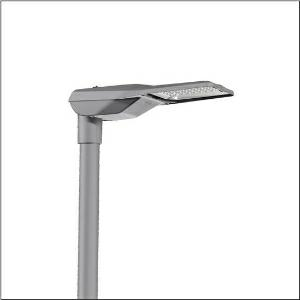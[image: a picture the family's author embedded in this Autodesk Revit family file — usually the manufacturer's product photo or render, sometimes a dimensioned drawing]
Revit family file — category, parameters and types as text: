
# Revit family: streetlight_sl_21_mini___pl52_5xe2h33s08hb_6ab9
name_source: partatom
category: Lighting Fixtures
units: mm (PartAtom-declared; Revit-internal decimal feet)

## family parameters
Cut with Voids When Loaded = No
Host = Face
Light Source = No
Part Type = Normal
Room Calculation Point = No
Round Connector Dimension = Use Diameter
Shared = No

## types (1)
- --- (1 x LED, 8890 lm, 66 W, 3000K)
    Apparent Load = 66 VA
    CIE Flux Codes = 27 59 98 100 100
    Color Rendering = 70
    Color Temperature = 3000K
    Default Elevation = 1800 mm
    Description = Streetlight SL 21 mini, mast luminaire, primary light control with lens, of PMMA, primary optical cover: cover, of toughened safety glass, transparent, light distribution: PL52, light emission: direct distribution, primary light characteristic: asymmetric, installation type: side-entry, post-top, LED, High Power LED, rated luminous flux: 8.890lm, luminous efficacy: 135lm/W, light colour: 730, colour temperature: 3000K, control gear: D4i, control: overheat protection, constant luminous flux control, time-dependent luminous flux control, flexible luminous flux parameterisation, pre-setting: logarithmic dimming characteristic, mains connection: 220..240V, AC, 50/60Hz, start of lifetime: 66W, end of service life: 69W, reduction: 30W, luminaire housing, of diecast aluminium, powder-coated, SITECO metallic grey (DB 702S), corrosivity category C5 high according to DIN EN ISO 12944, please order mast flange separately, inclination adjustable: 0°, 5°, 10°, 15°, sealing non-destructively replaceable, multi-level sealing system, length: 628mm, width: 235mm, height: 110mm, mast flange for spigot size: 42mm (side-entry): 5XC10008XM4, 60/48mm (side-entry/post-top): 5XC10108XM2, 76/60mm (side-entry/post-top): 5XC10108XM1, mounting height: 4..8m, Smart Interface above, protection rating (complete): IP66, insulation class (complete): insulation class II (safety insulation), certification: CE, ENEC, ENEC+, VDE, impact resistance: IK10, permissible operating ambient temperature for outdoor applications: -40..+50°C, standard-compliant lighting for roads and squares, packaging unit: 1 piece

Light Distribution: PL52
    Height = 110 mm
    Lamp = 1 x LED
    Lamp Light Flux = 8890 lm
    Lamp Power = 66 W
    Lamp count = 1
    Length = 625 mm
    Luminous efficacy = 135 lm/W
    Manufacturer = Siteco
    ModVariant = No
    Model = 5XE2H33S08HB
    Number of Poles = 1
    OnlyDefault = Yes
    Power Factor = 1
    Product Name = Streetlight SL 21 mini | PL52
    Product group = mast luminaire | pylon top
    ProductGroupID = 6100
    Protection Class = Protection class II
    Protection Degree = IP 66
    RLX_Detail_Level = 1
    RLX_Emergency_Light_Flux = 0 lm
    RLX_Emergency_Type = 0
    RLX_Emergency_Type_DB = No
    RlxData = <blob elided: 35717 chars, md5=4990cbbb>
    Socket = socket
    Standby Power = 0 W
    System Light Flux = 8890 lm
    System Power = 66 W
    Type Comments = factory setting: luminous flux: 100 % | dim-lin: 254 | 670 mA
    Type Image = l_1003515.jpg
    URL = http://relux.com
    VarID = @adj_187595
    Voltage = 0 V
    Weight = 0.00 kg
    Width = 234 mm

## geometry (parser evidence)
native form markers: Blend x4, Sweep x11
no freeform markers — native parametric forms only
